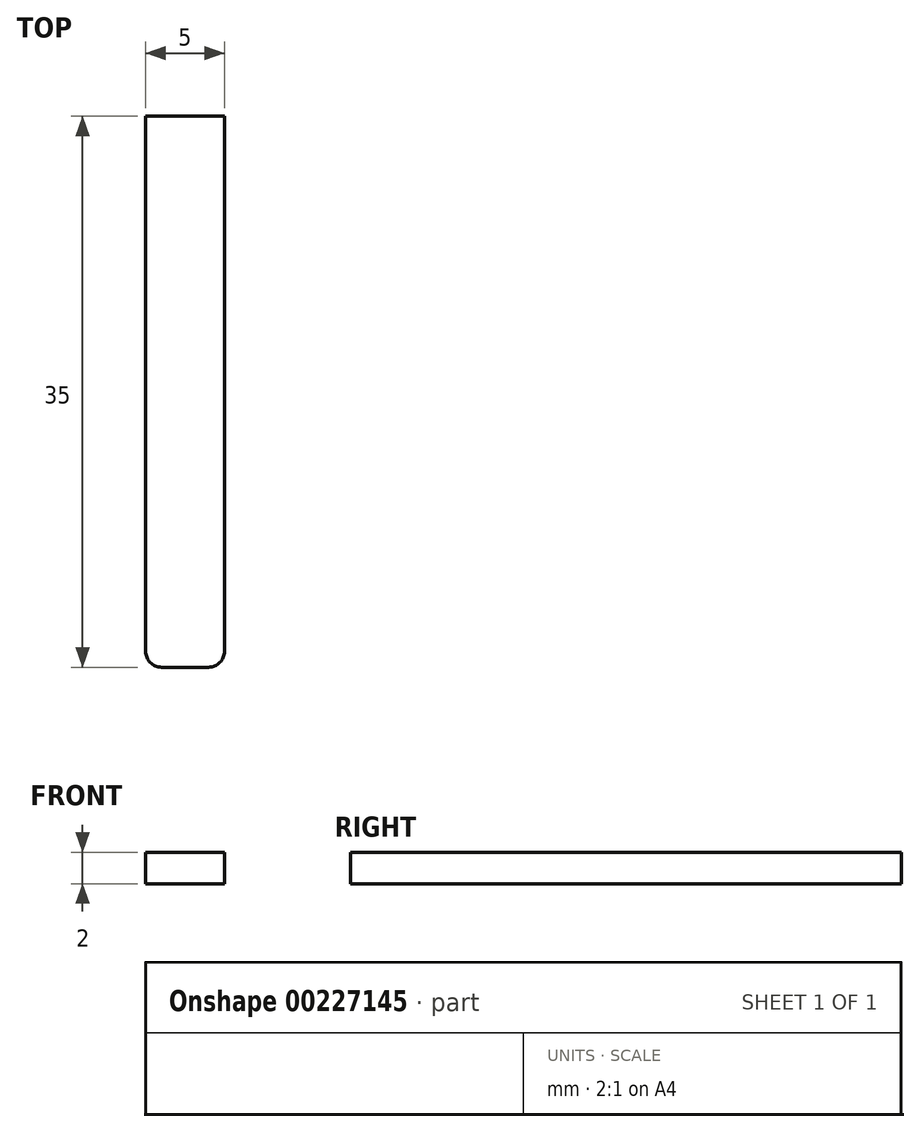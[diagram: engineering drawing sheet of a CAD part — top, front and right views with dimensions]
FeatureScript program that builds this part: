
annotation { "Feature Type Name" : "Feature", "Feature Type Description" : "" }
export const myFeature = defineFeature(function(context is Context, id is Id, definition is map)
    precondition{}
    {
        {
            var Q0;
            Q0=qCreatedBy(makeId("Top.planeOp"),FACE);
            var sketch = newSketch(context, id + "F0", { "sketchPlane" : qUnion([Q0])});
            skLineSegment(sketch, "E0.bottom", {"start": v(2.5, 17.5) * mm, "end": v(-2.5, 17.5) * mm});
            skLineSegment(sketch, "E0.top", {"start": v(1.5, -17.5) * mm, "end": v(-1.5, -17.5) * mm});
            skLineSegment(sketch, "E0.left", {"start": v(2.5, 17.5) * mm, "end": v(2.5, -16.5) * mm});
            skLineSegment(sketch, "E0.right", {"start": v(-2.5, 17.5) * mm, "end": v(-2.5, -16.5) * mm});
            skPoint(sketch, "E0.middle", {"position": v(0, 0) * mm});
            skPoint(sketch, "E1.visualSharp", {"position": v(-2.5, -17.5) * mm});
            skArc(sketch, "E1.filletArc", {"start": v(-2.5, -16.5) * mm, "mid": v(-2.2, -17.2) * mm, "end": v(-1.5, -17.5) * mm});
            skPoint(sketch, "E2.visualSharp", {"position": v(2.5, -17.5) * mm});
            skArc(sketch, "E2.filletArc", {"start": v(1.5, -17.5) * mm, "mid": v(2.2, -17.2) * mm, "end": v(2.5, -16.5) * mm});
            skSolve(sketch);
        }
        {
            var Q0;
            Q0 = qSketchRegion(id + "F0", true);
            extrude(context, id + "F1", {"entities" : qUnion([Q0]), "depth" : 2 * mm});
        }
    });
